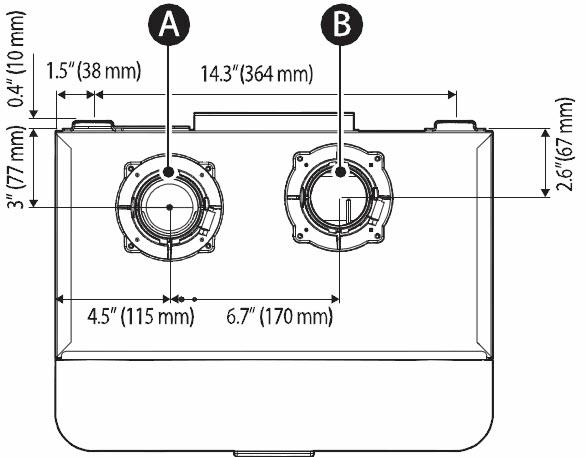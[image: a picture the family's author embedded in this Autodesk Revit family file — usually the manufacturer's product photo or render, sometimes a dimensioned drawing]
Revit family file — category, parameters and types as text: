
# Revit family: Water_Heater-Racks-Navien-NPE-4_Unit_Front-02
name_source: partatom
category: Mechanical Equipment
revit_build: Autodesk Revit 2016 (Build: 20150220_1215(x64)
units: mm (PartAtom-declared; Revit-internal decimal feet)

## family parameters
Cut with Voids When Loaded = No
Host = Face
OmniClass Number = 23.65.35.11
OmniClass Title = Supply Water Heaters
Part Type = Normal
Room Calculation Point = No
Round Connector Dimension = Use Diameter
Shared = No

## types (4) — shared parameters
2" Exhaust/Intake = Yes
3" Exhaust/Intake = No
Apparent Load = 0 VA
Assembly Code = D3010500
Certifications = Energy Star | AHRI | CSA | CSA | NFS
Cold Water Inlet = 1"
Configuration = NPE_F4_4F
Default Elevation = 48 "
Depth = 23.8 "
Description = 4 Unit Front
Exhaust = 2"
Finish = Metal - Navien - White
Flow Rate = 1 GPM
Flow Rate Note = 35°F (19°C) temp rise: 11.2 GPM (42 L/m) | 45°F (25°C) temp rise: 8.7 GPM (33 L/m) | 67°F (36°C) temp rise: NPE-240A: 5.6 GPM(21 L/m), NPE-240S: 5.7 GPM(22 L/m)
Frequency = 60 Hz
Gas Inlet = 1"
Heating Capacity = 120000.0 Btu/h
Heating Capacity Note = 19,900–199,900 (BTU/H)
Height = 65.5 "
Hot Water Outlet = 1"
Ignition = Electronic ignition
Installation Type = Indoor
Intake = 2"
Keynote = 22 33 00.A1
Manifold(s) = (1) 30019043A
Manufacturer = Navien, Inc.
Manufacturer Fax Number = (949) 420-0430
Natural Gas Manifold Pressure = -0.05" WC to -0.58" WC
Natural Gas Supply Pressure = 3.5"–10.5" WC
Number of Poles = 1
Phase = 1
Power Factor = 1
Product Documentation Link = https://www.navieninc.com
Product Name = NPE Series Tankless Water Heaters w/ Racks
Product Page URL = https://www.navieninc.com
Propane Gas Manifold Pressure = -0.10" WC to -0.78" WC
Propane Gas Supply Pressure = 8"–13" WC
Rack(s) = (1) GFFM-KDIZUS-003 + (3) GFFM-KDIZUS-004
Required Cascade Operation Accessory = (4) 30014367A (Common Vent Damper & Cascade Communication Cable) or (3) GXXX000546 (Individual Vent Cascade Communication Cable)
Type Comments = For Wall Mount RL Manifold systems- Exclude Base & Add-on Racks
URL = https://www.navieninc.com
Venting = Exhaust: 2" PVC, CPVC, PP, SS / 2" special gas vent type BH (Class II, A/B/C) | Intake: 2" PVC, CPVC, PP, SS / 2" special gas vent type BH (Class II, A/B/C) | Vent clearances: 0" to combustibles
Venting Type = Forced draft direct vent
Version = 2016 - v1.0.a
Voltage = 120 V
Water Pressure = 15–150 PSI
Wi-Fi Ready = NaviLink Wi-Fi Control: PBCM-AS-001
Width = 82.3 "

## per-type parameters (varying)
| type | Constraints | Model | Natural Gas | Propane Gas | Recirculation Inlet | Recirculation Inlet Visibility | Tankless Water Heaters | Weight |
| Natural Gas - Recirculating System - NPE-240A(Advanced)-NG | 6 | (4) NPE-240A-NG | Yes | No | 0" | Yes | (4) NPE-240A-NG | 82.00 lbf |
| Natural Gas - NPE-240S(Standard)-NG | 7 | (4) NPE-240S-NG | Yes | No | 1" | No | (4) NPE-240S-NG | 75.00 lbf |
| Propane Gas - Recirculating System - NPE-240A(Advanced)-LPG | 6 | (4) NPE-240A-LPG | No | Yes | 0" | Yes | (4) NPE-240A-LPG | 82.00 lbf |
| Propane Gas - NPE-240S(Standard)-LPG | 7 | (4) NPE-240S-LPG | No | Yes | 1" | No | (4) NPE-240S-LPG | 75.00 lbf |

## geometry (parser evidence)
native form markers: Sweep x15
no freeform markers — native parametric forms only
